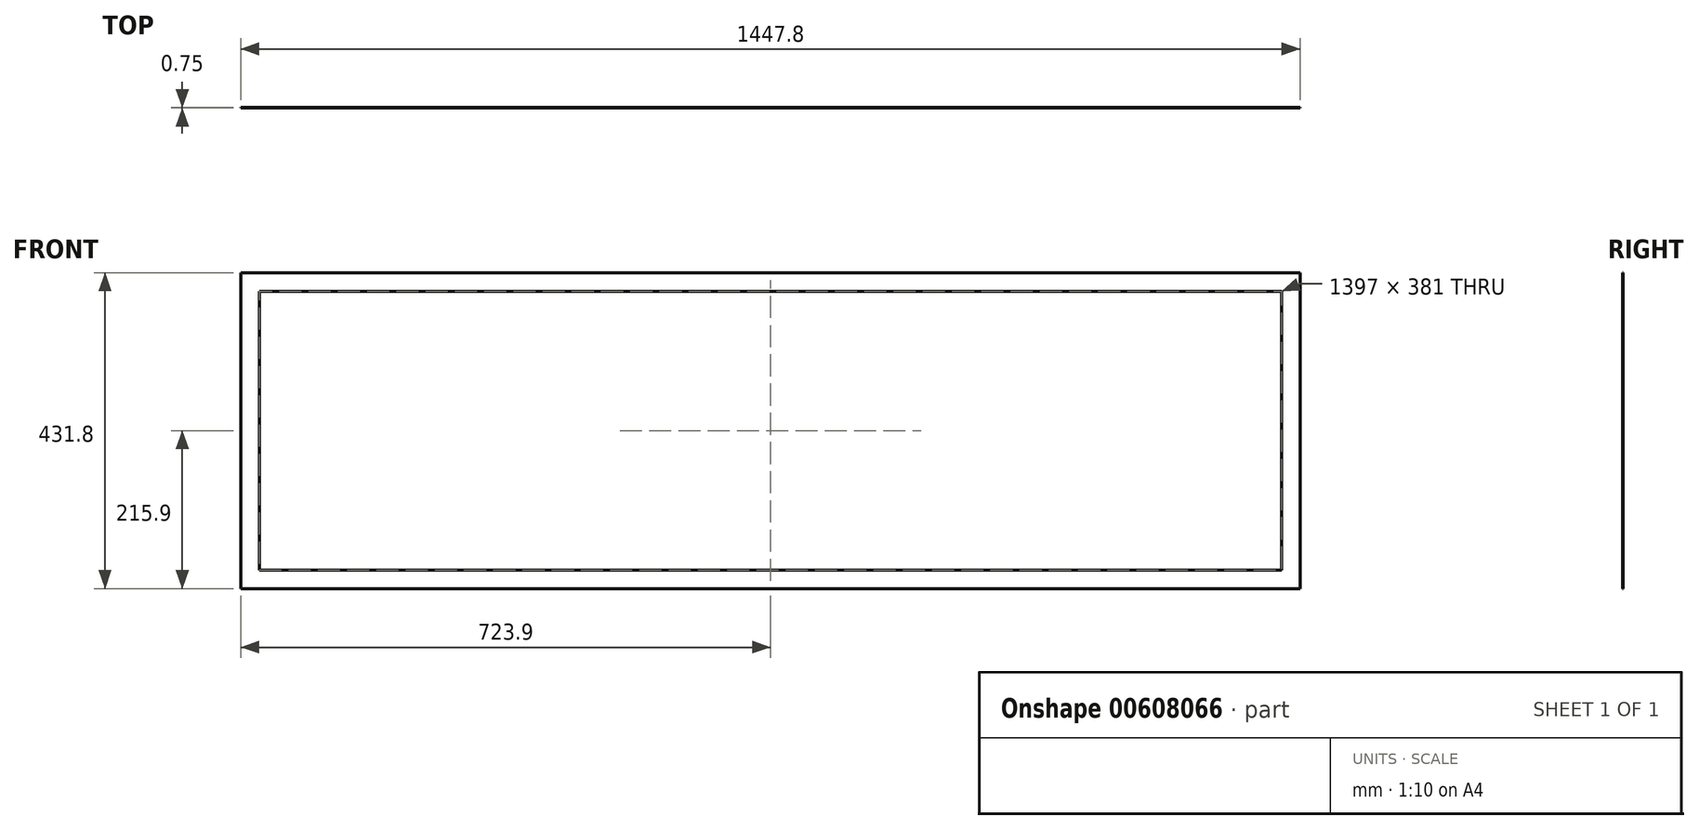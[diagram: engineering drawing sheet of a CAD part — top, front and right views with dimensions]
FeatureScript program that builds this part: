
annotation { "Feature Type Name" : "Feature", "Feature Type Description" : "" }
export const myFeature = defineFeature(function(context is Context, id is Id, definition is map)
    precondition{}
    {
        {
            assignVariable(context, id + "F0", {"name" : "Depth", "anyValue" : 0.75});
        }
        {
            var Q0;
            Q0=qCreatedBy(makeId("Front.planeOp"),FACE);
            var sketch = newSketch(context, id + "F1", { "sketchPlane" : qUnion([Q0])});
            skLineSegment(sketch, "E0.bottom", {"start": v(-723.9, -215.9) * mm, "end": v(723.9, -215.9) * mm});
            skLineSegment(sketch, "E0.top", {"start": v(-723.9, 215.9) * mm, "end": v(723.9, 215.9) * mm});
            skLineSegment(sketch, "E0.left", {"start": v(-723.9, -215.9) * mm, "end": v(-723.9, 215.9) * mm});
            skLineSegment(sketch, "E0.right", {"start": v(723.9, -215.9) * mm, "end": v(723.9, 215.9) * mm});
            skPoint(sketch, "E1", {"position": v(-723.9, 0) * mm});
            skPoint(sketch, "E2", {"position": v(0, 215.9) * mm});
            skLineSegment(sketch, "E3.0", {"start": v(-698.5, 190.5) * mm, "end": v(698.5, 190.5) * mm});
            skLineSegment(sketch, "E3.1", {"start": v(-698.5, -190.5) * mm, "end": v(-698.5, 190.5) * mm});
            skLineSegment(sketch, "E3.2", {"start": v(-698.5, -190.5) * mm, "end": v(698.5, -190.5) * mm});
            skLineSegment(sketch, "E3.3", {"start": v(698.5, -190.5) * mm, "end": v(698.5, 190.5) * mm});
            skLineSegment(sketch, "E4.bottom", {"start": v(-254, -190.5) * mm, "end": v(-228.6, -190.5) * mm});
            skLineSegment(sketch, "E4.top", {"start": v(-254, 190.5) * mm, "end": v(-228.6, 190.5) * mm});
            skLineSegment(sketch, "E4.left", {"start": v(-254, -190.5) * mm, "end": v(-254, 190.5) * mm});
            skLineSegment(sketch, "E4.right", {"start": v(-228.6, -190.5) * mm, "end": v(-228.6, 190.5) * mm});
            skLineSegment(sketch, "E5.bottom", {"start": v(228.6, -190.5) * mm, "end": v(254, -190.5) * mm});
            skLineSegment(sketch, "E5.top", {"start": v(228.6, 190.5) * mm, "end": v(254, 190.5) * mm});
            skLineSegment(sketch, "E5.left", {"start": v(228.6, -190.5) * mm, "end": v(228.6, 190.5) * mm});
            skLineSegment(sketch, "E5.right", {"start": v(254, -190.5) * mm, "end": v(254, 190.5) * mm});
            skPoint(sketch, "E6", {"position": v(-241.3, -190.5) * mm});
            skPoint(sketch, "E7", {"position": v(241.3, -190.5) * mm});
            skSolve(sketch);
        }
        {
            var Q0;
            Q0=makeQuery(id+"F1.imprint","IMPRINT",FACE,{"disambiguationData":[TD([[makeQuery(id+"F1.imprint","IMPRINT",EDGE,{"derivedFrom":sQuery(id+"F1.wireOp",EDGE,"E0.bottom")}),1.0]])]});
            var Q1;
            Q1=makeQuery(id+"F1.imprint","IMPRINT",FACE,{"disambiguationData":[TD([[makeQuery(id+"F1.imprint","IMPRINT",EDGE,{"derivedFrom":sQuery(id+"F1.wireOp",EDGE,"E4.bottom")}),1.0]])]});
            var Q2;
            Q2=makeQuery(id+"F1.imprint","IMPRINT",FACE,{"disambiguationData":[TD([[makeQuery(id+"F1.imprint","IMPRINT",EDGE,{"derivedFrom":sQuery(id+"F1.wireOp",EDGE,"E5.bottom")}),1.0]])]});
            extrude(context, id + "F2", {"entities" : qUnion([Q0, Q1, Q2]), "depth" : (getVariable(context, 'Depth')) * mm, "offsetDistance" : 25.4 * mm});
        }
    });
